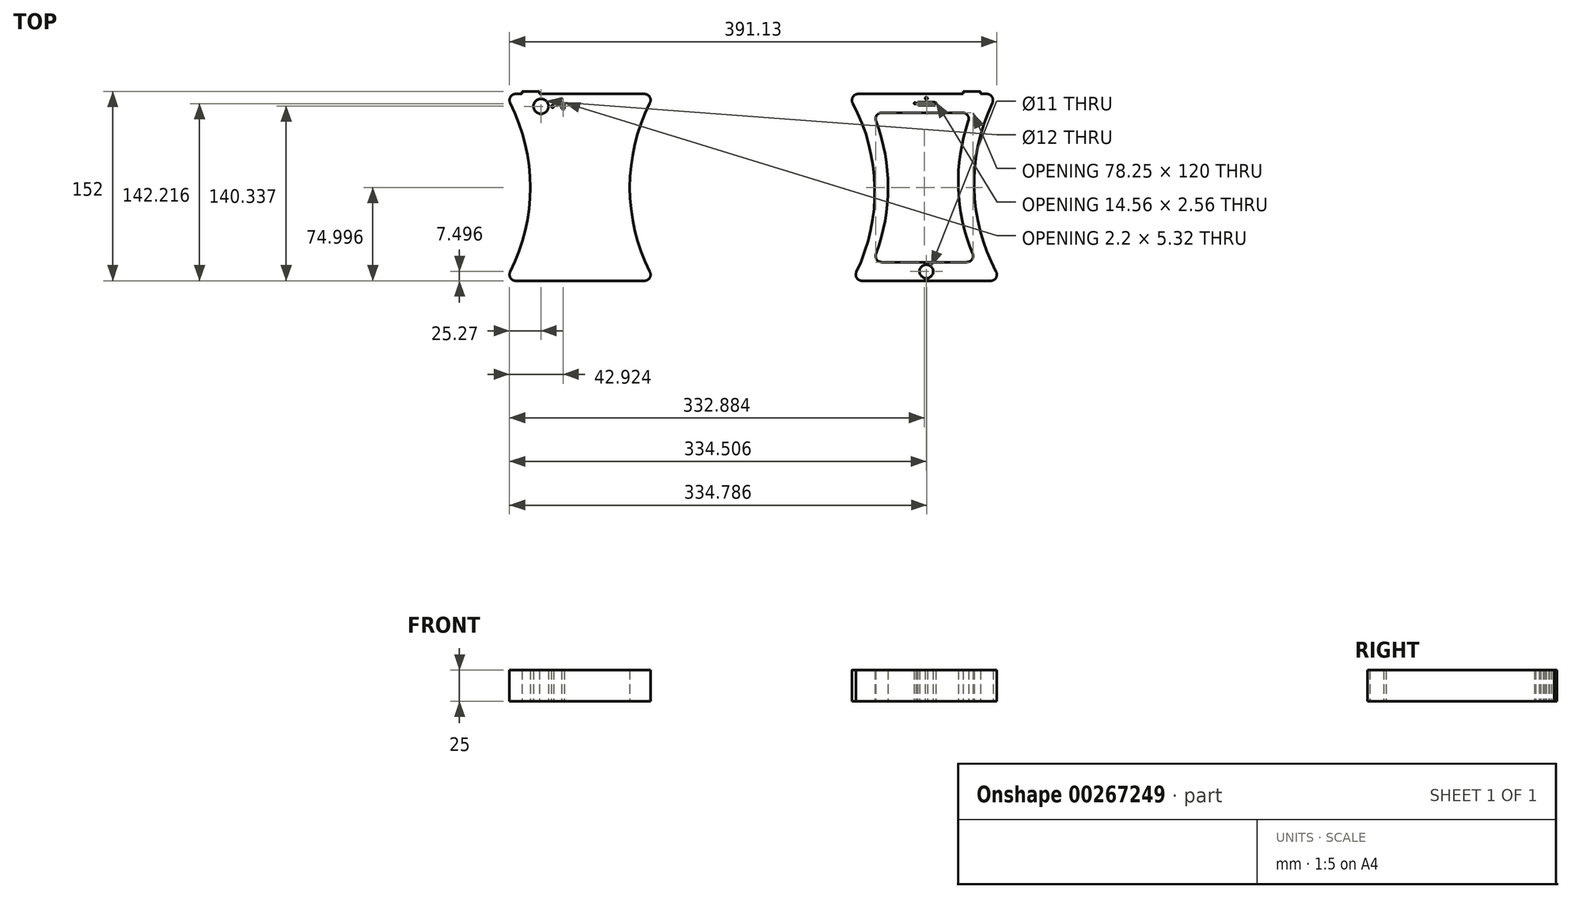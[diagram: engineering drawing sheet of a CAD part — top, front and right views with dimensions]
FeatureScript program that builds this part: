
annotation { "Feature Type Name" : "Feature", "Feature Type Description" : "" }
export const myFeature = defineFeature(function(context is Context, id is Id, definition is map)
    precondition{}
    {
        {
            var Q0;
            Q0=qCreatedBy(makeId("Top.planeOp"),FACE);
            var sketch = newSketch(context, id + "F0", { "sketchPlane" : qUnion([Q0])});
            skArc(sketch, "E0", {"start": v(-58.52, -73.87) * mm, "mid": v(-43.87, -5.76) * mm, "end": v(-61.55, 61.62) * mm});
            skLineSegment(sketch, "E1", {"start": v(-57.14, 68.98) * mm, "end": v(46.07, 68.98) * mm});
            skArc(sketch, "E2", {"start": v(50.58, 61.82) * mm, "mid": v(35.92, -6.29) * mm, "end": v(53.6, -73.67) * mm});
            skLineSegment(sketch, "E3", {"start": v(-54.01, -81.02) * mm, "end": v(49.2, -81.02) * mm});
            skPoint(sketch, "E4.visualSharp", {"position": v(-65.76, 68.98) * mm});
            skArc(sketch, "E4.filletArc", {"start": v(-57.14, 68.98) * mm, "mid": v(-61.43, 66.55) * mm, "end": v(-61.55, 61.62) * mm});
            skPoint(sketch, "E5.visualSharp", {"position": v(54.24, 68.98) * mm});
            skArc(sketch, "E5.filletArc", {"start": v(50.58, 61.82) * mm, "mid": v(50.3, 66.64) * mm, "end": v(46.07, 68.98) * mm});
            skPoint(sketch, "E6.visualSharp", {"position": v(-62.19, -81.02) * mm});
            skArc(sketch, "E6.filletArc", {"start": v(-58.52, -73.87) * mm, "mid": v(-58.24, -78.69) * mm, "end": v(-54.01, -81.02) * mm});
            skPoint(sketch, "E7.visualSharp", {"position": v(57.81, -81.02) * mm});
            skArc(sketch, "E7.filletArc", {"start": v(49.2, -81.02) * mm, "mid": v(53.48, -78.6) * mm, "end": v(53.6, -73.67) * mm});
            skLineSegment(sketch, "E8", {"start": v(30.1, -66.02) * mm, "end": v(-38.2, -66.02) * mm});
            skLineSegment(sketch, "E9", {"start": v(-38.2, 53.98) * mm, "end": v(26.58, 53.98) * mm});
            skArc(sketch, "E10", {"start": v(-42.88, -59.25) * mm, "mid": v(-33.12, -6.02) * mm, "end": v(-42.88, 47.2) * mm});
            skArc(sketch, "E11", {"start": v(31.31, 47.35) * mm, "mid": v(23.25, -6.19) * mm, "end": v(34.72, -59.1) * mm});
            skPoint(sketch, "E12.visualSharp", {"position": v(-45.64, 53.98) * mm});
            skArc(sketch, "E12.filletArc", {"start": v(-38.2, 53.98) * mm, "mid": v(-42.32, 51.82) * mm, "end": v(-42.88, 47.2) * mm});
            skPoint(sketch, "E13.visualSharp", {"position": v(33.76, 53.98) * mm});
            skArc(sketch, "E13.filletArc", {"start": v(31.31, 47.35) * mm, "mid": v(30.65, 51.88) * mm, "end": v(26.58, 53.98) * mm});
            skPoint(sketch, "E14.visualSharp", {"position": v(-45.64, -66.02) * mm});
            skArc(sketch, "E14.filletArc", {"start": v(-42.88, -59.25) * mm, "mid": v(-42.32, -63.86) * mm, "end": v(-38.2, -66.02) * mm});
            skPoint(sketch, "E15.visualSharp", {"position": v(37.81, -66.02) * mm});
            skArc(sketch, "E15.filletArc", {"start": v(30.1, -66.02) * mm, "mid": v(34.26, -63.8) * mm, "end": v(34.72, -59.1) * mm});
            skCircle(sketch, "E16", {"center": v(-2.42, -73.52) * mm, "radius": 5.5 * mm});
            skLineSegment(sketch, "E17", {"start": v(-8.42, 62.48) * mm, "end": v(4.14, 62.48) * mm});
            skLineSegment(sketch, "E18", {"start": v(4.14, 59.92) * mm, "end": v(-8.42, 59.92) * mm});
            skLineSegment(sketch, "E19", {"start": v(5.14, 61.48) * mm, "end": v(5.14, 60.92) * mm});
            skLineSegment(sketch, "E20", {"start": v(-9.42, 61.48) * mm, "end": v(-9.42, 60.92) * mm});
            skCircle(sketch, "E21", {"center": v(-2.42, 65.48) * mm, "radius": 1 * mm});
            skCircle(sketch, "E22", {"center": v(-11.42, 61.48) * mm, "radius": 0.75 * mm});
            skPoint(sketch, "E23.visualSharp", {"position": v(-9.42, 59.92) * mm});
            skArc(sketch, "E23.filletArc", {"start": v(-9.42, 60.92) * mm, "mid": v(-9.13, 60.2) * mm, "end": v(-8.42, 59.92) * mm});
            skPoint(sketch, "E24.visualSharp", {"position": v(-9.42, 62.48) * mm});
            skArc(sketch, "E24.filletArc", {"start": v(-8.42, 62.48) * mm, "mid": v(-9.13, 62.18) * mm, "end": v(-9.42, 61.48) * mm});
            skPoint(sketch, "E25.visualSharp", {"position": v(5.14, 62.48) * mm});
            skArc(sketch, "E25.filletArc", {"start": v(5.14, 61.48) * mm, "mid": v(4.84, 62.18) * mm, "end": v(4.14, 62.48) * mm});
            skPoint(sketch, "E26.visualSharp", {"position": v(5.14, 59.92) * mm});
            skArc(sketch, "E26.filletArc", {"start": v(4.14, 59.92) * mm, "mid": v(4.84, 60.2) * mm, "end": v(5.14, 60.92) * mm});
            skLineSegment(sketch, "E27", {"start": v(-331.93, -81.02) * mm, "end": v(-228.7, -81.02) * mm});
            skArc(sketch, "E28", {"start": v(-224.25, 61.72) * mm, "mid": v(-240.41, -6.02) * mm, "end": v(-224.25, -73.77) * mm});
            skArc(sketch, "E29", {"start": v(-336.39, -73.77) * mm, "mid": v(-320.22, -6.02) * mm, "end": v(-336.39, 61.72) * mm});
            skLineSegment(sketch, "E30", {"start": v(-228.7, 68.98) * mm, "end": v(-331.93, 68.98) * mm});
            skPoint(sketch, "E31.visualSharp", {"position": v(-340.32, 68.98) * mm});
            skArc(sketch, "E31.filletArc", {"start": v(-331.93, 68.98) * mm, "mid": v(-336.19, 66.6) * mm, "end": v(-336.39, 61.72) * mm});
            skPoint(sketch, "E32.visualSharp", {"position": v(-220.32, 68.98) * mm});
            skArc(sketch, "E32.filletArc", {"start": v(-224.25, 61.72) * mm, "mid": v(-224.45, 66.6) * mm, "end": v(-228.7, 68.98) * mm});
            skPoint(sketch, "E33.visualSharp", {"position": v(-220.32, -81.02) * mm});
            skArc(sketch, "E33.filletArc", {"start": v(-228.7, -81.02) * mm, "mid": v(-224.45, -78.64) * mm, "end": v(-224.25, -73.77) * mm});
            skPoint(sketch, "E34.visualSharp", {"position": v(-340.32, -81.02) * mm});
            skArc(sketch, "E34.filletArc", {"start": v(-336.39, -73.77) * mm, "mid": v(-336.19, -78.64) * mm, "end": v(-331.93, -81.02) * mm});
            skPoint(sketch, "E35.startSnap0", {"position": v(-320.22, -6.02) * mm});
            skPoint(sketch, "E36.visualSharp", {"position": v(-320.22, 53.98) * mm});
            skPoint(sketch, "E37.visualSharp", {"position": v(-236.8, 62.72) * mm});
            skPoint(sketch, "E38.visualSharp", {"position": v(-236.8, -57.28) * mm});
            skPoint(sketch, "E39.visualSharp", {"position": v(-323.72, -57.28) * mm});
            skCircle(sketch, "E40", {"center": v(-311.66, 58.98) * mm, "radius": 6 * mm});
            skCircle(sketch, "E41", {"center": v(-302.37, 58.98) * mm, "radius": 1 * mm});
            skLineSegment(sketch, "E42", {"start": v(-295.1, 60.98) * mm, "end": v(-295.1, 57.66) * mm});
            skLineSegment(sketch, "E43", {"start": v(-294.1, 61.98) * mm, "end": v(-293.9, 61.98) * mm});
            skLineSegment(sketch, "E44", {"start": v(-292.9, 60.98) * mm, "end": v(-292.9, 57.66) * mm});
            skLineSegment(sketch, "E45", {"start": v(-293.9, 56.66) * mm, "end": v(-294.1, 56.66) * mm});
            skPoint(sketch, "E46.visualSharp", {"position": v(-292.9, 56.66) * mm});
            skArc(sketch, "E46.filletArc", {"start": v(-293.9, 56.66) * mm, "mid": v(-293.2, 56.95) * mm, "end": v(-292.9, 57.66) * mm});
            skPoint(sketch, "E47.visualSharp", {"position": v(-295.1, 56.66) * mm});
            skArc(sketch, "E47.filletArc", {"start": v(-295.1, 57.66) * mm, "mid": v(-294.81, 56.95) * mm, "end": v(-294.1, 56.66) * mm});
            skPoint(sketch, "E48.visualSharp", {"position": v(-292.9, 61.98) * mm});
            skArc(sketch, "E48.filletArc", {"start": v(-292.9, 60.98) * mm, "mid": v(-293.2, 61.68) * mm, "end": v(-293.9, 61.98) * mm});
            skPoint(sketch, "E49.visualSharp", {"position": v(-295.1, 61.98) * mm});
            skArc(sketch, "E49.filletArc", {"start": v(-294.1, 61.98) * mm, "mid": v(-294.81, 61.68) * mm, "end": v(-295.1, 60.98) * mm});
            skLineSegment(sketch, "E50", {"start": v(-326.93, 68.98) * mm, "end": v(-326.93, 70.98) * mm});
            skLineSegment(sketch, "E51", {"start": v(-326.93, 70.98) * mm, "end": v(-312.93, 70.98) * mm});
            skLineSegment(sketch, "E52", {"start": v(-312.93, 70.98) * mm, "end": v(-312.93, 68.98) * mm});
            skLineSegment(sketch, "E53", {"start": v(41.07, 68.98) * mm, "end": v(41.07, 70.98) * mm});
            skLineSegment(sketch, "E54", {"start": v(41.07, 70.98) * mm, "end": v(27.07, 70.98) * mm});
            skLineSegment(sketch, "E55", {"start": v(27.07, 70.98) * mm, "end": v(27.07, 68.98) * mm});
            skSolve(sketch);
        }
        {
            var Q0;
            {var subQ0=sQuery(id+"F0.wireOp",EDGE,"E53");Q0=makeQuery(id+"F0.imprint","IMPRINT",FACE,{"disambiguationData":[TD([[makeQuery(id+"F0.imprint","IMPRINT",EDGE,{"derivedFrom":subQ0}),1.0]])]});}
            var Q1;
            {var subQ0=sQuery(id+"F0.wireOp",EDGE,"E50");Q1=makeQuery(id+"F0.imprint","IMPRINT",FACE,{"disambiguationData":[TD([[makeQuery(id+"F0.imprint","IMPRINT",EDGE,{"derivedFrom":subQ0}),-1.0]])]});}
            var Q2;
            Q2=makeQuery(id+"F0.imprint","IMPRINT",FACE,{"disambiguationData":[TD([[makeQuery(id+"F0.imprint","IMPRINT",EDGE,{"derivedFrom":sQuery(id+"F0.wireOp",EDGE,"E27")}),1.0]])]});
            var Q3;
            Q3=makeQuery(id+"F0.imprint","IMPRINT",FACE,{"disambiguationData":[TD([[makeQuery(id+"F0.imprint","IMPRINT",EDGE,{"derivedFrom":sQuery(id+"F0.wireOp",EDGE,"E0")}),-1.0]])]});
            extrude(context, id + "F1", {"entities" : qUnion([Q0, Q1, Q2, Q3]), "depth" : 25 * mm});
        }
    });
